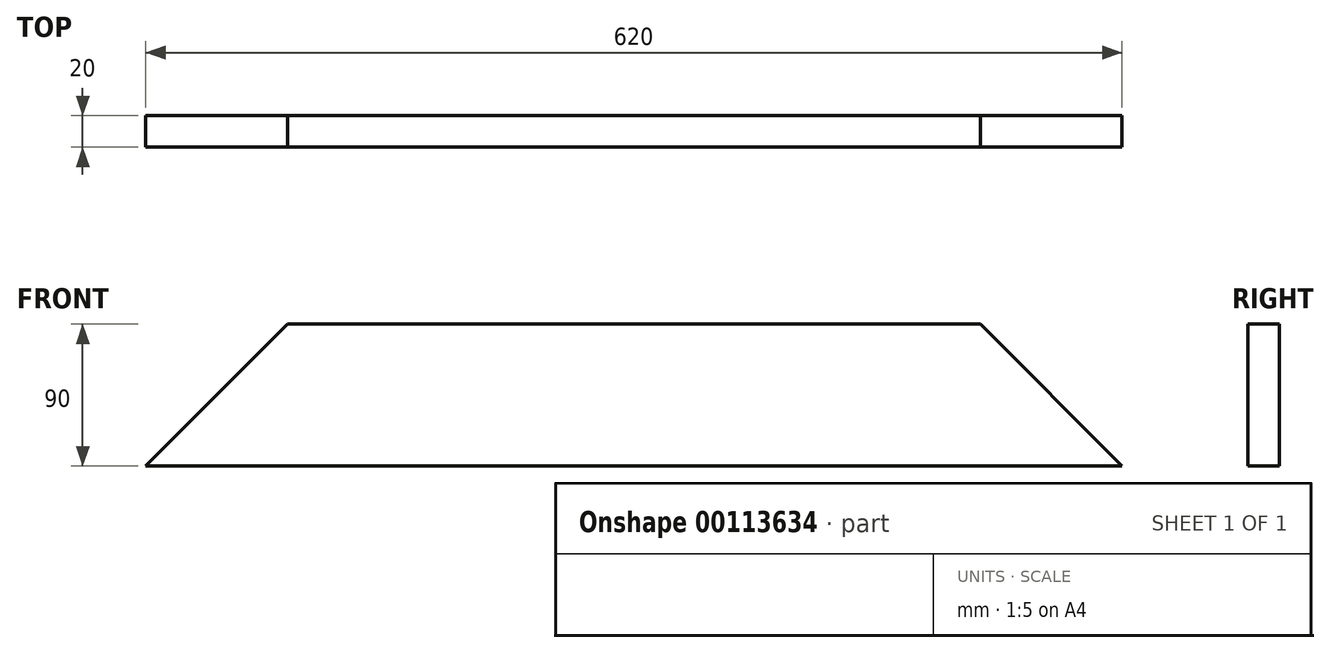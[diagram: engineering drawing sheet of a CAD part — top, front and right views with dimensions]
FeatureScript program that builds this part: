
annotation { "Feature Type Name" : "Feature", "Feature Type Description" : "" }
export const myFeature = defineFeature(function(context is Context, id is Id, definition is map)
    precondition{}
    {
        {
            var Q0;
            Q0=qCreatedBy(makeId("Front.planeOp"),FACE);
            var sketch = newSketch(context, id + "F0", { "sketchPlane" : qUnion([Q0])});
            skLineSegment(sketch, "E0.bottom", {"start": v(-250, 0) * mm, "end": v(370, 0) * mm});
            skLineSegment(sketch, "E0.top", {"start": v(-160, 90) * mm, "end": v(280, 90) * mm});
            skLineSegment(sketch, "E1", {"start": v(-250, 0) * mm, "end": v(-160, 90) * mm});
            skLineSegment(sketch, "E2", {"start": v(370, 0) * mm, "end": v(280, 90) * mm});
            skSolve(sketch);
        }
        {
            var Q0;
            Q0=makeQuery(id+"F0.imprint","IMPRINT",FACE,{"disambiguationData":[TD([[makeQuery(id+"F0.imprint","IMPRINT",EDGE,{"derivedFrom":sQuery(id+"F0.wireOp",EDGE,"E0.bottom")}),1.0]])]});
            extrude(context, id + "F1", {"entities" : qUnion([Q0]), "depth" : 20 * mm});
        }
    });
